# Revit family: KEUCO_14944000110
name_source: partatom
category: Allgemeines Modell
revit_build: Autodesk Revit 2016 (Build: 20150220_1215(x64)
units: mm (PartAtom-declared; Revit-internal decimal feet)

## family parameters
Arbeitsebenenbasiert = Ja
Beim Laden mit Abzugskörper schneiden = Nein
Bemaßung runder Anschluss = Durchmesser verwenden
Gemeinsam genutzt = Nein
Immer vertikal = Nein
Kann Basisbauteil für Bewehrung sein = Nein
Raumberechnungspunkt = Nein
Teiletyp = Normal

## types (9) — shared parameters
Hersteller = KEUCO
Höhe = 2000 mm  [stored 6.56168 ft]
Serie = Plan
Typenbild = <Keine Auswahl>
URL = https://www.keuco.com
Verwendung = DU / WA
zero-valued in all types: Gewicht

## per-type parameters (varying)
| type | Ausschreibungstext | Längetyp | Material | Vorgabe-Ansicht |
| 14944000110 | KEUCO PLAN Duschvorhang PLAN uni 14944000110 
1400 x 2000 mm, weiß/8 Ösen
100 % Trevira, 80 g/m²
seitlich gesäumt, Verstärkungsband für Edelstahlösen
Abstand der Ösen ca. 20 cm
Edelstahl-Rollsaum auf rechts genäht, per Meter 50 g
duschdicht, fungizid, antibakteriell, antistatisch, 
kalandert, bei 30 Grad waschbar, Einlaufquote 1-2 %
schadstoffgeprüft nach Öko-Tex-Standard 100
komplett mit Vorhangringen, weiß

Hinweis zu den Maßen:
Bei den angegeben Maßen handelt es sich um fertige Vorhangmaße.
Damit der Vorhang nicht im Wannenboden 
oder auf dem Fußboden aufliegt, empfehlen wir: 
Abstand vom Duschvorhang zum Boden ca. 30 mm. 
Abstand zwischen Stangenmitte und Oberkante Duschvorhang ca. 40 mm.

Die Vorhangbreite sollte ca. das 1,3 bis 1,5-fache 
der Vorhangstangenlänge betragen. | 1 | weiß/8 Ösen | 1800 mm  [stored 5.90551 ft] |
| 14944000120 | KEUCO PLAN Duschvorhang PLAN uni 14944000120 
2000 x 2000 mm, weiß/11 Ösen
100 % Trevira, 80 g/m²
seitlich gesäumt, Verstärkungsband für Edelstahlösen
Abstand der Ösen ca. 20 cm
Edelstahl-Rollsaum auf rechts genäht, per Meter 50 g
duschdicht, fungizid, antibakteriell, antistatisch, 
kalandert, bei 30 Grad waschbar, Einlaufquote 1-2 %
schadstoffgeprüft nach Öko-Tex-Standard 100
komplett mit Vorhangringen, weiß

Hinweis zu den Maßen:
Bei den angegeben Maßen handelt es sich um fertige Vorhangmaße.
Damit der Vorhang nicht im Wannenboden 
oder auf dem Fußboden aufliegt, empfehlen wir: 
Abstand vom Duschvorhang zum Boden ca. 30 mm. 
Abstand zwischen Stangenmitte und Oberkante Duschvorhang ca. 40 mm.

Die Vorhangbreite sollte ca. das 1,3 bis 1,5-fache 
der Vorhangstangenlänge betragen. | 2 | weiß/11 Ösen | 0 mm  [stored 0 ft] |
| 14944000130 | KEUCO PLAN Duschvorhang PLAN uni 14944000130 
3000 x 2000 mm, weiß/16 Ösen
100 % Trevira, 80 g/m²
seitlich gesäumt, Verstärkungsband für Edelstahlösen
Abstand der Ösen ca. 20 cm
Edelstahl-Rollsaum auf rechts genäht, per Meter 50 g
duschdicht, fungizid, antibakteriell, antistatisch, 
kalandert, bei 30 Grad waschbar, Einlaufquote 1-2 %
schadstoffgeprüft nach Öko-Tex-Standard 100
komplett mit Vorhangringen, weiß

Hinweis zu den Maßen:
Bei den angegeben Maßen handelt es sich um fertige Vorhangmaße.
Damit der Vorhang nicht im Wannenboden 
oder auf dem Fußboden aufliegt, empfehlen wir: 
Abstand vom Duschvorhang zum Boden ca. 30 mm. 
Abstand zwischen Stangenmitte und Oberkante Duschvorhang ca. 40 mm.

Die Vorhangbreite sollte ca. das 1,3 bis 1,5-fache 
der Vorhangstangenlänge betragen. | 3 | ecru/8 Ösen | 0 mm  [stored 0 ft] |
| 14944000210 | KEUCO PLAN Duschvorhang PLAN uni 14944000210 
1400 x 2000 mm, ecru/8 Ösen
100 % Trevira, 80 g/m²
seitlich gesäumt, Verstärkungsband für Edelstahlösen
Abstand der Ösen ca. 20 cm
Edelstahl-Rollsaum auf rechts genäht, per Meter 50 g
duschdicht, fungizid, antibakteriell, antistatisch, 
kalandert, bei 30 Grad waschbar, Einlaufquote 1-2 %
schadstoffgeprüft nach Öko-Tex-Standard 100
komplett mit Vorhangringen, weiß

Hinweis zu den Maßen:
Bei den angegeben Maßen handelt es sich um fertige Vorhangmaße.
Damit der Vorhang nicht im Wannenboden 
oder auf dem Fußboden aufliegt, empfehlen wir: 
Abstand vom Duschvorhang zum Boden ca. 30 mm. 
Abstand zwischen Stangenmitte und Oberkante Duschvorhang ca. 40 mm.

Die Vorhangbreite sollte ca. das 1,3 bis 1,5-fache 
der Vorhangstangenlänge betragen. | 1 | ecru/8 Ösen | 0 mm  [stored 0 ft] |
| 14944000220 | KEUCO PLAN Duschvorhang PLAN uni 14944000220 
2000 x 2000 mm, ecru/11 Ösen
100 % Trevira, 80 g/m²
seitlich gesäumt, Verstärkungsband für Edelstahlösen
Abstand der Ösen ca. 20 cm
Edelstahl-Rollsaum auf rechts genäht, per Meter 50 g
duschdicht, fungizid, antibakteriell, antistatisch, 
kalandert, bei 30 Grad waschbar, Einlaufquote 1-2 %
schadstoffgeprüft nach Öko-Tex-Standard 100
komplett mit Vorhangringen, weiß

Hinweis zu den Maßen:
Bei den angegeben Maßen handelt es sich um fertige Vorhangmaße.
Damit der Vorhang nicht im Wannenboden 
oder auf dem Fußboden aufliegt, empfehlen wir: 
Abstand vom Duschvorhang zum Boden ca. 30 mm. 
Abstand zwischen Stangenmitte und Oberkante Duschvorhang ca. 40 mm.

Die Vorhangbreite sollte ca. das 1,3 bis 1,5-fache 
der Vorhangstangenlänge betragen. | 2 | ecru/11 Ösen | 0 mm  [stored 0 ft] |
| 14944000230 | KEUCO PLAN Duschvorhang PLAN uni 14944000230 
3000 x 2000 mm, ecru/16 Ösen
100 % Trevira, 80 g/m²
seitlich gesäumt, Verstärkungsband für Edelstahlösen
Abstand der Ösen ca. 20 cm
Edelstahl-Rollsaum auf rechts genäht, per Meter 50 g
duschdicht, fungizid, antibakteriell, antistatisch, 
kalandert, bei 30 Grad waschbar, Einlaufquote 1-2 %
schadstoffgeprüft nach Öko-Tex-Standard 100
komplett mit Vorhangringen, weiß

Hinweis zu den Maßen:
Bei den angegeben Maßen handelt es sich um fertige Vorhangmaße.
Damit der Vorhang nicht im Wannenboden 
oder auf dem Fußboden aufliegt, empfehlen wir: 
Abstand vom Duschvorhang zum Boden ca. 30 mm. 
Abstand zwischen Stangenmitte und Oberkante Duschvorhang ca. 40 mm.

Die Vorhangbreite sollte ca. das 1,3 bis 1,5-fache 
der Vorhangstangenlänge betragen. | 3 | ecru/16 Ösen | 0 mm  [stored 0 ft] |
| 14944000310 | KEUCO PLAN Duschvorhang PLAN uni 14944000310 
1400 x 2000 mm, lichtgrau/8 Ösen
100 % Trevira, 80 g/m²
seitlich gesäumt, Verstärkungsband für Edelstahlösen
Abstand der Ösen ca. 20 cm
Edelstahl-Rollsaum auf rechts genäht, per Meter 50 g
duschdicht, fungizid, antibakteriell, antistatisch, 
kalandert, bei 30 Grad waschbar, Einlaufquote 1-2 %
schadstoffgeprüft nach Öko-Tex-Standard 100
komplett mit Vorhangringen, weiß

Hinweis zu den Maßen:
Bei den angegeben Maßen handelt es sich um fertige Vorhangmaße.
Damit der Vorhang nicht im Wannenboden 
oder auf dem Fußboden aufliegt, empfehlen wir: 
Abstand vom Duschvorhang zum Boden ca. 30 mm. 
Abstand zwischen Stangenmitte und Oberkante Duschvorhang ca. 40 mm.

Die Vorhangbreite sollte ca. das 1,3 bis 1,5-fache 
der Vorhangstangenlänge betragen. | 1 | lichtgrau/8 Ösen | 0 mm  [stored 0 ft] |
| 14944000320 | KEUCO PLAN Duschvorhang PLAN uni 14944000320 
2000 x 2000 mm, lichtgrau/11 Ösen
100 % Trevira, 80 g/m²
seitlich gesäumt, Verstärkungsband für Edelstahlösen
Abstand der Ösen ca. 20 cm
Edelstahl-Rollsaum auf rechts genäht, per Meter 50 g
duschdicht, fungizid, antibakteriell, antistatisch, 
kalandert, bei 30 Grad waschbar, Einlaufquote 1-2 %
schadstoffgeprüft nach Öko-Tex-Standard 100
komplett mit Vorhangringen, weiß

Hinweis zu den Maßen:
Bei den angegeben Maßen handelt es sich um fertige Vorhangmaße.
Damit der Vorhang nicht im Wannenboden 
oder auf dem Fußboden aufliegt, empfehlen wir: 
Abstand vom Duschvorhang zum Boden ca. 30 mm. 
Abstand zwischen Stangenmitte und Oberkante Duschvorhang ca. 40 mm.

Die Vorhangbreite sollte ca. das 1,3 bis 1,5-fache 
der Vorhangstangenlänge betragen. | 2 | lichtgrau/11 Ösen | 0 mm  [stored 0 ft] |
| 14944000330 | KEUCO PLAN Duschvorhang PLAN uni 14944000330 
3000 x 2000 mm, lichtgrau/16 Ösen
100 % Trevira, 80 g/m²
seitlich gesäumt, Verstärkungsband für Edelstahlösen
Abstand der Ösen ca. 20 cm
Edelstahl-Rollsaum auf rechts genäht, per Meter 50 g
duschdicht, fungizid, antibakteriell, antistatisch, 
kalandert, bei 30 Grad waschbar, Einlaufquote 1-2 %
schadstoffgeprüft nach Öko-Tex-Standard 100
komplett mit Vorhangringen, weiß

Hinweis zu den Maßen:
Bei den angegeben Maßen handelt es sich um fertige Vorhangmaße.
Damit der Vorhang nicht im Wannenboden 
oder auf dem Fußboden aufliegt, empfehlen wir: 
Abstand vom Duschvorhang zum Boden ca. 30 mm. 
Abstand zwischen Stangenmitte und Oberkante Duschvorhang ca. 40 mm.

Die Vorhangbreite sollte ca. das 1,3 bis 1,5-fache 
der Vorhangstangenlänge betragen. | 3 | lichtgrau/16 Ösen | 0 mm  [stored 0 ft] |

note: column(s) folded — value = type name in every type: Artikelnummer

note: [stored X ft] marks values corroborated as IEEE doubles in the binary element streams (Revit-internal decimal feet)

## geometry (parser evidence)
native form markers: Blend x4, Sweep x3
no freeform markers — native parametric forms only
